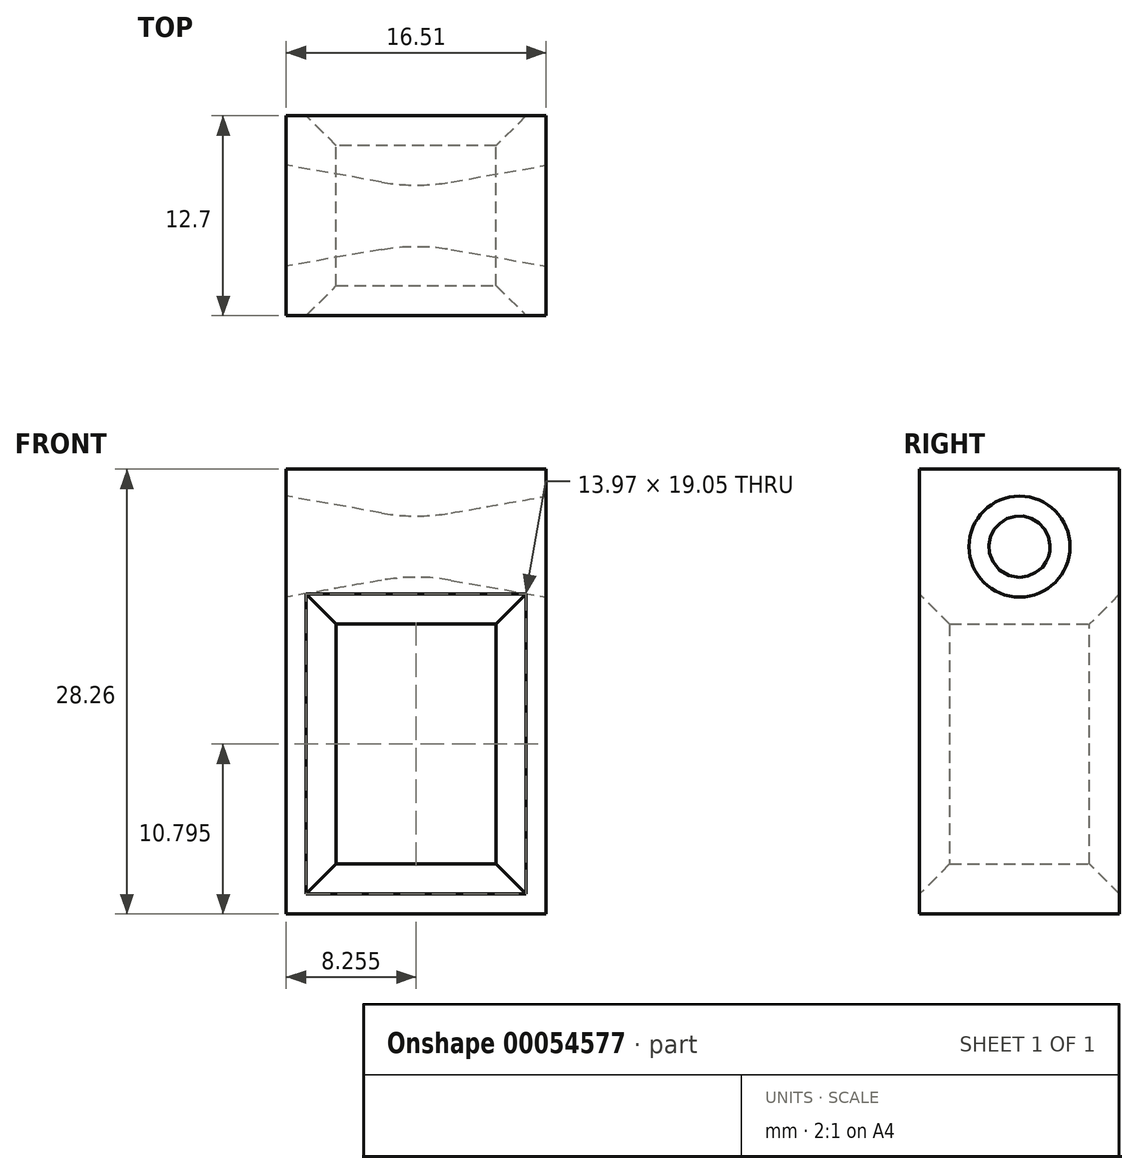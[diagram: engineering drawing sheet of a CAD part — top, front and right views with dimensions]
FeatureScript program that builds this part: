
annotation { "Feature Type Name" : "Feature", "Feature Type Description" : "" }
export const myFeature = defineFeature(function(context is Context, id is Id, definition is map)
    precondition{}
    {
        {
            var Q0;
            Q0=qCreatedBy(makeId("Front.planeOp"),FACE);
            var sketch = newSketch(context, id + "F0", { "sketchPlane" : qUnion([Q0])});
            skLineSegment(sketch, "E0.bottom", {"start": v(0, 0) * mm, "end": v(16.51, 0) * mm});
            skLineSegment(sketch, "E0.top", {"start": v(0, 28.27) * mm, "end": v(16.51, 28.27) * mm});
            skLineSegment(sketch, "E0.left", {"start": v(0, 0) * mm, "end": v(0, 28.26) * mm});
            skLineSegment(sketch, "E0.right", {"start": v(16.51, 0) * mm, "end": v(16.51, 28.26) * mm});
            skLineSegment(sketch, "E1.bottom", {"start": v(3.18, 3.18) * mm, "end": v(13.34, 3.18) * mm});
            skLineSegment(sketch, "E1.top", {"start": v(3.17, 18.41) * mm, "end": v(13.34, 18.41) * mm});
            skLineSegment(sketch, "E1.left", {"start": v(3.18, 3.18) * mm, "end": v(3.17, 18.41) * mm});
            skLineSegment(sketch, "E1.right", {"start": v(13.34, 3.18) * mm, "end": v(13.34, 18.41) * mm});
            skLineSegment(sketch, "E2", {"start": v(8.25, 25.09) * mm, "end": v(8.26, 21.59) * mm, "construction": true});
            skPoint(sketch, "E3", {"position": v(8.25, 28.27) * mm});
            skSolve(sketch);
        }
        {
            var Q0;
            Q0 = qSketchRegion(id + "F0", true);
            extrude(context, id + "F1", {"entities" : qUnion([Q0]), "endBound" : BoundingType.SYMMETRIC, "depth" : 12.7 * mm});
        }
        {
            var Q0;
            Q0=makeQuery(id+"F1.opExtrude","CAP_EDGE",EDGE,{"disambiguationData":[OSD([sQuery(id+"F0.wireOp",EDGE,"E1.right")])],"isStart":false});
            var Q1;
            Q1=makeQuery(id+"F1.opExtrude","CAP_EDGE",EDGE,{"disambiguationData":[OSD([sQuery(id+"F0.wireOp",EDGE,"E1.top")])],"isStart":false});
            var Q2;
            Q2=makeQuery(id+"F1.opExtrude","CAP_EDGE",EDGE,{"disambiguationData":[OSD([sQuery(id+"F0.wireOp",EDGE,"E1.left")])],"isStart":false});
            var Q3;
            Q3=makeQuery(id+"F1.opExtrude","CAP_EDGE",EDGE,{"disambiguationData":[OSD([sQuery(id+"F0.wireOp",EDGE,"E1.bottom")])],"isStart":false});
            var Q4;
            Q4=makeQuery(id+"F1.opExtrude","CAP_EDGE",EDGE,{"disambiguationData":[OSD([sQuery(id+"F0.wireOp",EDGE,"E1.left")])],"isStart":true});
            var Q5;
            Q5=makeQuery(id+"F1.opExtrude","CAP_EDGE",EDGE,{"disambiguationData":[OSD([sQuery(id+"F0.wireOp",EDGE,"E1.top")])],"isStart":true});
            var Q6;
            Q6=makeQuery(id+"F1.opExtrude","CAP_EDGE",EDGE,{"disambiguationData":[OSD([sQuery(id+"F0.wireOp",EDGE,"E1.bottom")])],"isStart":true});
            var Q7;
            Q7=makeQuery(id+"F1.opExtrude","CAP_EDGE",EDGE,{"disambiguationData":[OSD([sQuery(id+"F0.wireOp",EDGE,"E1.right")])],"isStart":true});
            chamfer(context, id + "F2", {"entities" : qUnion([Q0, Q1, Q2, Q3, Q4, Q5, Q6, Q7]), "width" : 1.9 * mm, "tangentPropagation" : true});
        }
        {
            var Q0;
            Q0=makeQuery(id+"F1.opExtrude","SWEPT_FACE",FACE,{"disambiguationData":[OSD([sQuery(id+"F0.wireOp",EDGE,"E0.left")])]});
            var Q1;
            Q1=makeQuery(id+"F1.opExtrude","SWEPT_FACE",FACE,{"disambiguationData":[OSD([sQuery(id+"F0.wireOp",EDGE,"E0.right")])]});
            cPlane(context, id + "F3", {"entities" : qUnion([Q0, Q1]), "cplaneType" : CPlaneType.MID_PLANE, "offset" : 152.4 * mm, "width" : 152.4 * mm, "height" : 152.4 * mm});
        }
        {
            var Q0;
            Q0=qCreatedBy(id+"F3.planeOp",FACE);
            var sketch = newSketch(context, id + "F4", { "sketchPlane" : qUnion([Q0])});
            skCircle(sketch, "E4", {"center": v(0, 23.34) * mm, "radius": 1.75 * mm});
            skSolve(sketch);
        }
        {
            var Q0;
            Q0 = qSketchRegion(id + "F4", true);
            extrude(context, id + "F5", {"entities" : qUnion([Q0]), "operationType" : NewBodyOperationType.REMOVE, "endBound" : BoundingType.SYMMETRIC, "oppositeDirection" : true, "depth" : 25.4 * mm, "hasDraft" : true, "draftAngle" : 10 * degree});
        }
        {
            var Q0;
            {var subQ0=makeQuery(id+"F5.opExtrude","SWEPT_FACE",FACE,{"disambiguationData":[OSD([sQuery(id+"F4.wireOp",EDGE,"E4")])]});Q0=makeQuery(id+"F5.boolean.opBoolean","COPY",EDGE,{"derivedFrom":makeQuery(id+"F5.*.booleanUnion.opBoolean","MERGE",EDGE,{"derivedFrom":[makeQuery(id+"F5.*.split.splitOp","SPLIT_SURFACE_INTERSECT",EDGE,{"derivedFrom":[subQ0]}),makeQuery(id+"F5.*.split.splitOp","SPLIT_SURFACE_INTERSECT",EDGE,{"derivedFrom":[subQ0],"isFromBackBody":true})]})});}
            fillet(context, id + "F6", {"entities" : qUnion([Q0]), "radius" : 12.7 * mm, "tangentPropagation" : true, "allowEdgeOverflow" : false});
        }
    });
